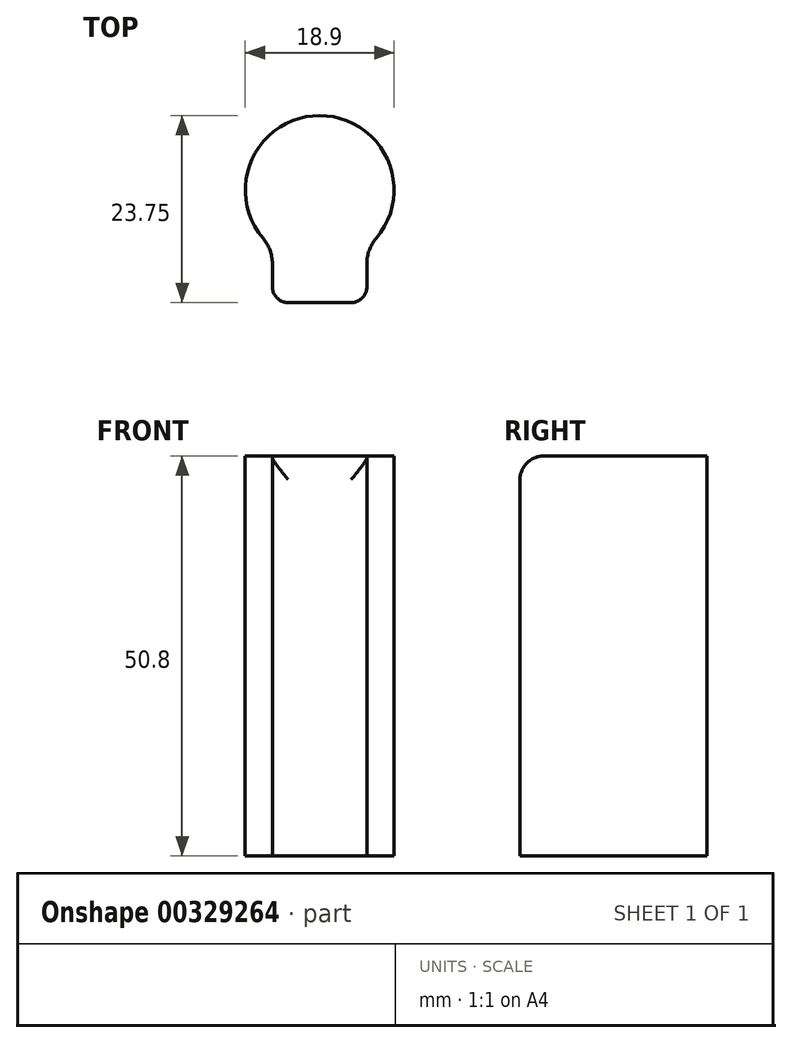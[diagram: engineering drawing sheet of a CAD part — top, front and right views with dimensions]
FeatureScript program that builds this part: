
annotation { "Feature Type Name" : "Feature", "Feature Type Description" : "" }
export const myFeature = defineFeature(function(context is Context, id is Id, definition is map)
    precondition{}
    {
        {
            var Q0;
            Q0=qCreatedBy(makeId("Top.planeOp"),FACE);
            var sketch = newSketch(context, id + "F0", { "sketchPlane" : qUnion([Q0])});
            skCircle(sketch, "E0", {"center": v(0, 0) * mm, "radius": 9.45 * mm});
            skLineSegment(sketch, "E1", {"start": v(0, -14.3) * mm, "end": v(-6, -14.3) * mm});
            skLineSegment(sketch, "E2", {"start": v(0, -14.3) * mm, "end": v(6, -14.3) * mm});
            skLineSegment(sketch, "E3", {"start": v(-6, -14.3) * mm, "end": v(-6, -7.3) * mm});
            skLineSegment(sketch, "E4", {"start": v(6, -14.3) * mm, "end": v(6, -7.3) * mm});
            skSolve(sketch);
        }
        {
            var Q0;
            {var subQ0=sQuery(id+"F0.wireOp",EDGE,"E0");var subQ1=makeQuery(id+"F0.imprint","INTERSECT",VERTEX,{"derivedFrom":[subQ0,sQuery(id+"F0.wireOp",EDGE,"E3")]});Q0=makeQuery(id+"F0.imprint","IMPRINT",FACE,{"disambiguationData":[TD([[makeQuery(id+"F0.imprint","IMPRINT",EDGE,{"disambiguationData":[TD([[subQ1,-1.0]])],"derivedFrom":subQ0}),1.0]])]});}
            var Q1;
            Q1=makeQuery(id+"F0.imprint","IMPRINT",FACE,{"disambiguationData":[TD([[makeQuery(id+"F0.imprint","IMPRINT",EDGE,{"derivedFrom":sQuery(id+"F0.wireOp",EDGE,"E1")}),-1.0]])]});
            extrude(context, id + "F1", {"entities" : qUnion([Q0, Q1]), "depth" : 50.8 * mm});
        }
        {
            var Q0;
            Q0=makeQuery(id+"F1.opExtrude","SWEPT_EDGE",EDGE,{"disambiguationData":[OSD([sQuery(id+"F0.wireOp",EDGE,"E2"),sQuery(id+"F0.wireOp",EDGE,"E4")])]});
            var Q1;
            Q1=makeQuery(id+"F1.opExtrude","SWEPT_EDGE",EDGE,{"disambiguationData":[OSD([sQuery(id+"F0.wireOp",EDGE,"E1"),sQuery(id+"F0.wireOp",EDGE,"E3")])]});
            fillet(context, id + "F2", {"entities" : qUnion([Q0, Q1]), "radius" : 2 * mm, "tangentPropagation" : true, "allowEdgeOverflow" : false});
        }
        {
            var Q0;
            Q0=makeQuery(id+"F1.opExtrude","SWEPT_EDGE",EDGE,{"disambiguationData":[OSD([sQuery(id+"F0.wireOp",EDGE,"E0"),sQuery(id+"F0.wireOp",EDGE,"E3")])]});
            var Q1;
            Q1=makeQuery(id+"F1.opExtrude","SWEPT_EDGE",EDGE,{"disambiguationData":[OSD([sQuery(id+"F0.wireOp",EDGE,"E0"),sQuery(id+"F0.wireOp",EDGE,"E4")])]});
            fillet(context, id + "F3", {"entities" : qUnion([Q0, Q1]), "radius" : 5 * mm, "tangentPropagation" : true, "allowEdgeOverflow" : false});
        }
        {
            var Q0;
            Q0=makeQuery(id+"F1.opExtrude","CAP_EDGE",EDGE,{"disambiguationData":[OSD([sQuery(id+"F0.wireOp",EDGE,"E1"),sQuery(id+"F0.wireOp",EDGE,"E2")])],"isStart":false});
            fillet(context, id + "F4", {"entities" : qUnion([Q0]), "radius" : 3 * mm, "allowEdgeOverflow" : false});
        }
    });
